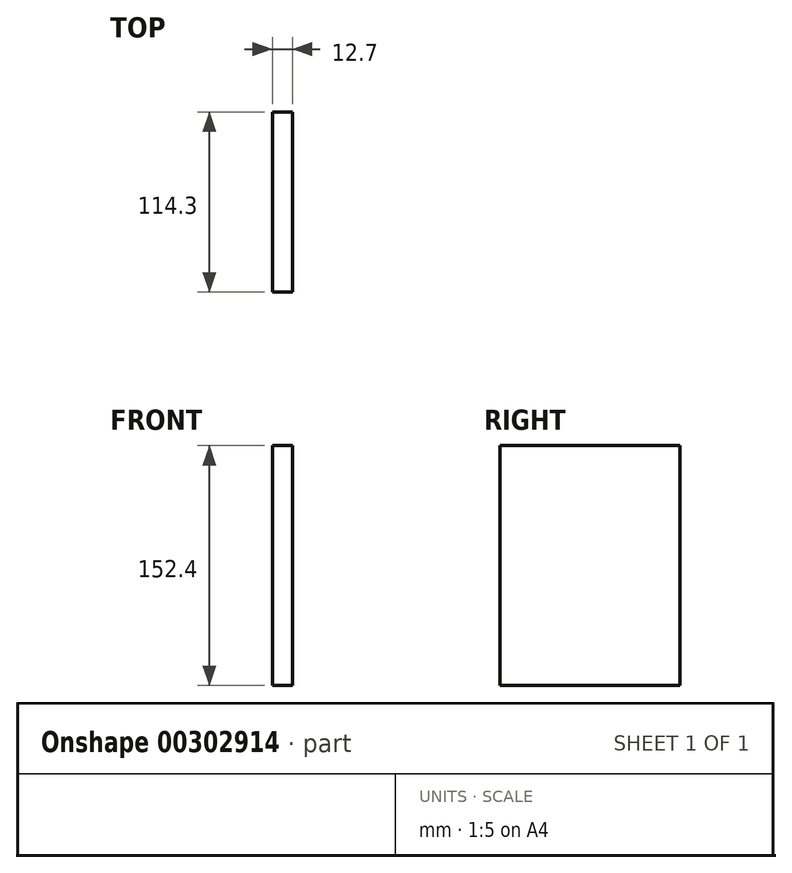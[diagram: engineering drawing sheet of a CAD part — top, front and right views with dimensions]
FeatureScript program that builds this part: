
annotation { "Feature Type Name" : "Feature", "Feature Type Description" : "" }
export const myFeature = defineFeature(function(context is Context, id is Id, definition is map)
    precondition{}
    {
        {
            var Q0;
            Q0=qCreatedBy(makeId("Right.planeOp"),FACE);
            var sketch = newSketch(context, id + "F0", { "sketchPlane" : qUnion([Q0])});
            skLineSegment(sketch, "E0.bottom", {"start": v(57.15, 76.2) * mm, "end": v(-57.15, 76.2) * mm});
            skLineSegment(sketch, "E0.top", {"start": v(57.15, -76.2) * mm, "end": v(-57.15, -76.2) * mm});
            skLineSegment(sketch, "E0.left", {"start": v(57.15, 76.2) * mm, "end": v(57.15, -76.2) * mm});
            skLineSegment(sketch, "E0.right", {"start": v(-57.15, 76.2) * mm, "end": v(-57.15, -76.2) * mm});
            skPoint(sketch, "E0.middle", {"position": v(0, 0) * mm});
            skSolve(sketch);
        }
        {
            var Q0;
            Q0=makeQuery(id+"F0.imprint","IMPRINT",FACE,{"disambiguationData":[TD([[makeQuery(id+"F0.imprint","IMPRINT",EDGE,{"derivedFrom":sQuery(id+"F0.wireOp",EDGE,"E0.bottom")}),1.0]])]});
            extrude(context, id + "F1", {"entities" : qUnion([Q0]), "depth" : 12.7 * mm});
        }
    });
